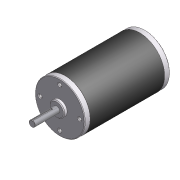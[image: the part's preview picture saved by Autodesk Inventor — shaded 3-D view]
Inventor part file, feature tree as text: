
AUTODESK INVENTOR PART (.ipt)
format: ipt  version: 2013 (Build 170138000, 138)  size: 198,144 bytes
history: native  units: mm (DEFAULTED — no unit token found)
features: sketch x9, extrude x7, chamfer x4, hole x2, pattern_circular x2, fillet x2
ambient origin geometry x8: Origin, YZ Plane, XZ Plane, XY Plane, X Axis, Y Axis, Z Axis, Center Point
bodies: Solid1 (feature_tree)
feature tree (26):
  extrude  "Extrusion1"  Depth=7.0mm TaperAngle=0.0deg
  extrude  "Extrusion2"  Depth=3.9878mm TaperAngle=0.0deg
  chamfer  "Chamfer1"  Distance=1.0mm
  hole  "Hole2"  [1 undecoded]
  pattern_circular  "Circular Pattern2"  Count=4 Angle=90.0deg
  chamfer  "Chamfer3"  Distance=31.623mm
  extrude  "Extrusion3"  Depth=12.7mm
  fillet  "Fillet1"  Radius=2.0mm
  extrude  "Extrusion4"  Depth=25.6286mm TaperAngle=0.0deg
  extrude  "Extrusion5"  Depth=95.6056mm TaperAngle=0.0deg
  extrude  "Extrusion6"  Depth=7.0mm TaperAngle=0.0deg
  extrude  "Extrusion7"  Depth=4.1148mm TaperAngle=0.0deg
  hole  "Hole3"  [1 undecoded]
  chamfer  "Chamfer2"  Distance=0.762mm
  pattern_circular  "Circular Pattern3"  [2 undecoded]
  fillet  "Fillet2"  Radius=20.0mm
  chamfer  "Chamfer4"  Distance=0.25mm
  sketch  "Sketch1"  dims[d0=64.008mm d1=7.0mm d2=0.0mm]
  sketch  "Sketch2"  dims[d3=19.05mm d4=3.9878mm d5=0.0mm d6=1.0mm d7=1.0mm]
  sketch  "Sketch4"  dims[d18=3.9624mm d19=9.525mm d20=6.35mm d21=60.0deg d22=19.05mm d23=20.594885mm d24=25.4mm d25=40.0mm d27=90.0deg]
  sketch  "Sketch5"  dims[d28=7.9502mm d29=31.623mm d30=0.0mm]
  sketch  "Sketch7"  dims[d31=0.79375mm d33=12.7mm d34=2.0mm]
  sketch  "Sketch8"  dims[d35=3.0mm d36=25.6286mm d37=0.0mm]
  sketch  "Sketch9"  dims[d38=64.4144mm d39=95.6056mm d40=0.0mm]
  sketch  "Sketch10"  dims[d41=64.008mm d42=7.0mm d43=0.0mm]
  sketch  "Sketch11"  dims[d44=30.1498mm d45=4.1148mm d46=0.0mm d47=5.08mm d48=12.7mm d49=9.906mm d50=4.572mm d51=14.3117mm d52=7.62mm d53=20.594885mm d54=0.508mm d55=3.175mm d56=0.762mm d57=0.762mm d58=3.175mm d59=20.0mm d61=360.0deg d62=0.25mm d63=3.175mm d64=45.0deg d65=45.0deg d66=45.0deg d67=45.0deg]
note: 4 required parameter values undecoded (feature->parameter linkage not recoverable at this tier; creation-order binding heuristic only, values carry confidence <= 0.55)
